# Revit family: VENTS-VK_EC
name_source: partatom
category: Mechanical Equipment
units: mm (PartAtom-declared; Revit-internal decimal feet)

## family parameters
Always vertical = No
Classification = None
Cut with Voids When Loaded = No
OmniClass Number = 23.75.35.17.11
OmniClass Title = Fans for Air Ductwork
Part Type = Breaks Into
Room Calculation Point = No
Round Connector Dimension = Use Diameter
Shared = No
Work Plane-Based = No

## types (6) — shared parameters
Current = 1 A
Description = Inline centrifugal fan for round ducts
Family Version = 1.0
Fan Material = Plastic White Glazed
Load Classification = HVAC
Maintenance Zone Height = 600 mm
Maintenance Zone Length = 600 mm
Maintenance Zone Material = Maintenance Zone
Maintenance Zone Width = 600 mm
Manufacturer = Vents
Number of Poles = 1
Power Factor = 1
Protection rating = IPX4
R11 = 5 mm  [stored 0.0164042 ft]
R12 = 15 mm  [stored 0.0492126 ft]
R21 = 5 mm  [stored 0.0164042 ft]
R22 = 15 mm  [stored 0.0492126 ft]
Transported Air Temperature (°C) = -25...+60
URL = https://ventilation-system.com
Voltage = 230 V

## per-type parameters (varying)
| type | Apparent Power | BoxA | BoxAngle | BoxD | BoxDepth | D | D1 | Duct Connection Size | L | L1 | L12 | L13 | L2 | L22 | L23 | Maximum Air Flow | Noise Level at 3 m (dBa) | Power | R1 | RPM (min-1) | Type Comments | Weight |
| VK 100 EC | 82 VA | 85 mm  [stored 0.278871 ft] | 90.00° | 304 mm | 74 mm  [stored 0.242782 ft] | 100 mm  [stored 0.328084 ft] | 250 mm  [stored 0.82021 ft] | 100 mm  [stored 0.328084 ft] | 230 mm  [stored 0.754593 ft] | 26 mm | 40 mm  [stored 0.131234 ft] | 40 mm  [stored 0.131234 ft] | 32 mm  [stored 0.104987 ft] | 73 mm | 19 mm  [stored 0.062336 ft] | 340 m³/h | 40 | 82 W | 125 mm  [stored 0.410105 ft] | 3400 | Inline centrifugal fan VK 100 EC | 2.00 kg |
| VK 125 EC | 84 VA | 85 mm  [stored 0.278871 ft] | 90.00° | 304 mm | 74 mm  [stored 0.242782 ft] | 125 mm  [stored 0.410105 ft] | 250 mm  [stored 0.82021 ft] | 125 mm  [stored 0.410105 ft] | 220 mm  [stored 0.721785 ft] | 38 mm  [stored 0.124672 ft] | 28 mm  [stored 0.0918635 ft] | 40 mm  [stored 0.131234 ft] | 32 mm  [stored 0.104987 ft] | 63 mm | 19 mm  [stored 0.062336 ft] | 420 m³/h | 42 | 84 W | 125 mm  [stored 0.410105 ft] | 3600 | Inline centrifugal fan VK 125 EC | 2.20 kg |
| VK 150 EC | 82 VA | 85 mm  [stored 0.278871 ft] | 90.00° | 350 mm | 85 mm  [stored 0.278871 ft] | 150 mm | 300 mm | 150 mm | 286 mm | 58 mm  [stored 0.190289 ft] | 16 mm  [stored 0.0524934 ft] | 48 mm  [stored 0.15748 ft] | 65 mm  [stored 0.213255 ft] | 70 mm | 29 mm  [stored 0.0951444 ft] | 630 m³/h | 45 | 82 W | 150 mm | 3400 | Inline centrifugal fan VK 150 EC | 2.50 kg |
| VK 200 EC | 84 VA | 120 mm  [stored 0.393701 ft] | 60.00° | 390 mm | 82 mm  [stored 0.269029 ft] | 200 mm  [stored 0.656168 ft] | 340 mm | 200 mm  [stored 0.656168 ft] | 276 mm  [stored 0.905512 ft] | 25 mm  [stored 0.082021 ft] | 26 mm | 68 mm | 28 mm  [stored 0.0918635 ft] | 101 mm | 28 mm  [stored 0.0918635 ft] | 885 m³/h | 47 | 84 W | 170 mm  [stored 0.557743 ft] | 2700 | Inline centrifugal fan VK 200 EC | 3.00 kg |
| VK 250 EC | 165 VA | 120 mm  [stored 0.393701 ft] | 60.00° | 390 mm | 82 mm  [stored 0.269029 ft] | 250 mm  [stored 0.82021 ft] | 340 mm | 250 mm  [stored 0.82021 ft] | 265 mm  [stored 0.869423 ft] | 28 mm  [stored 0.0918635 ft] | 26 mm | 55 mm  [stored 0.180446 ft] | 65 mm  [stored 0.213255 ft] | 63 mm | 28 mm  [stored 0.0918635 ft] | 1250 m³/h | 48 | 165 W | 170 mm  [stored 0.557743 ft] | 2600 | Inline centrifugal fan VK 250 EC | 4.30 kg |
| VK 315 EC | 165 VA | 120 mm  [stored 0.393701 ft] | 120.00° | 452 mm | 82 mm  [stored 0.269029 ft] | 315 mm | 400 mm | 315 mm | 276 mm  [stored 0.905512 ft] | 56 mm  [stored 0.183727 ft] | 31 mm  [stored 0.101706 ft] | 62 mm  [stored 0.203412 ft] | 38 mm  [stored 0.124672 ft] | 57 mm | 32 mm  [stored 0.104987 ft] | 1500 m³/h | 48 | 165 W | 200 mm  [stored 0.656168 ft] | 2500 | Inline centrifugal fan VK 315 EC | 4.90 kg |

note: column(s) folded — value = type name in every type: Model

note: [stored X ft] marks values corroborated as IEEE doubles in the binary element streams (Revit-internal decimal feet)

## geometry (parser evidence)
native form markers: Sweep x7
no freeform markers — native parametric forms only
